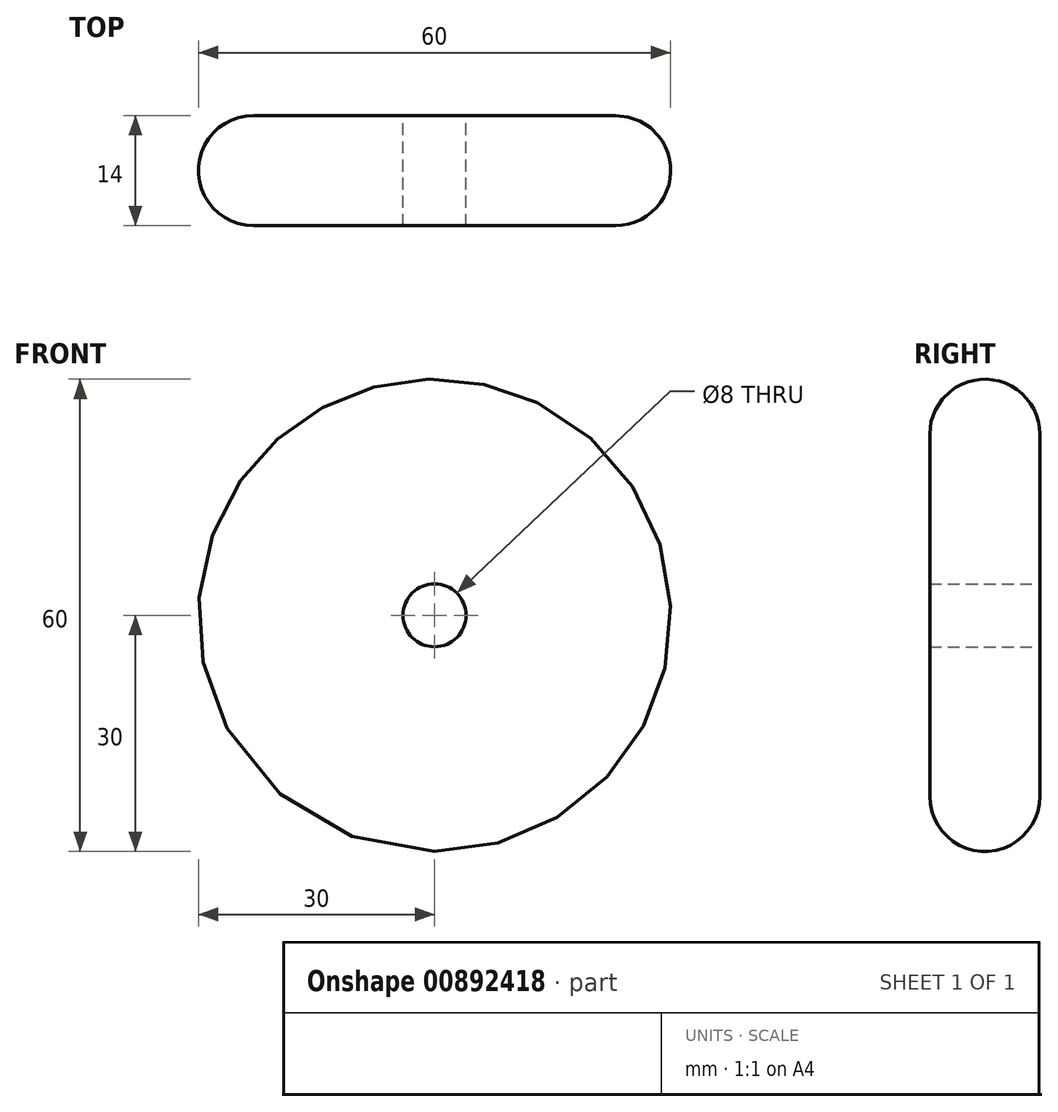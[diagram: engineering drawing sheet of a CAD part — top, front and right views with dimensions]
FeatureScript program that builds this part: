
annotation { "Feature Type Name" : "Feature", "Feature Type Description" : "" }
export const myFeature = defineFeature(function(context is Context, id is Id, definition is map)
    precondition{}
    {
        {
            var Q0;
            Q0=qCreatedBy(makeId("Front.planeOp"),FACE);
            var sketch = newSketch(context, id + "F0", { "sketchPlane" : qUnion([Q0])});
            skCircle(sketch, "E0", {"center": v(0, 0) * mm, "radius": 30 * mm});
            skSolve(sketch);
        }
        {
            var Q0;
            Q0=makeQuery(id+"F0.imprint","IMPRINT",FACE,{"disambiguationData":[TD([[makeQuery(id+"F0.imprint","IMPRINT",EDGE,{"derivedFrom":sQuery(id+"F0.wireOp",EDGE,"E0")}),1.0]])]});
            extrude(context, id + "F1", {"entities" : qUnion([Q0]), "depth" : 14 * mm, "offsetDistance" : 25 * mm});
        }
        {
            var Q0;
            Q0=makeQuery(id+"F1.opExtrude","CAP_EDGE",EDGE,{"disambiguationData":[OSD([sQuery(id+"F0.wireOp",EDGE,"E0")])],"isStart":false});
            var Q1;
            Q1=makeQuery(id+"F1.opExtrude","CAP_EDGE",EDGE,{"disambiguationData":[OSD([sQuery(id+"F0.wireOp",EDGE,"E0")])],"isStart":true});
            fillet(context, id + "F2", {"entities" : qUnion([Q0, Q1]), "radius" : 7 * mm, "tangentPropagation" : true, "allowEdgeOverflow" : false});
        }
        {
            var Q0;
            Q0=makeQuery(id+"F1.opExtrude","CAP_FACE",FACE,{"disambiguationData":[OSD([sQuery(id+"F0.wireOp",EDGE,"E0")])],"isStart":true});
            var sketch = newSketch(context, id + "F3", { "sketchPlane" : qUnion([Q0])});
            skCircle(sketch, "E1", {"center": v(0, 0) * mm, "radius": 3.87 * mm});
            skSolve(sketch);
        }
        {
            var Q0;
            Q0=sQuery(id+"F3.wireOp",VERTEX,"E1.center");
            var Q1;
            Q1=makeQuery(id+"F1.opExtrude","SWEPT_BODY",BODY,{"disambiguationData":[OSD([sQuery(id+"F0.wireOp",EDGE,"E0")])]});
            hole(context, id + "F4", {"style" : HoleStyle.SIMPLE, "endStyle" : HoleEndStyle.BLIND, "holeDiameter" : 8 * mm, "majorDiameter" : 5 * mm, "holeDepth" : 100 * mm, "isTappedThrough" : true, "tappedDepth" : 12 * mm, "tapClearance" : 3, "locations" : qUnion([Q0]), "scope" : qUnion([Q1])});
        }
    });
